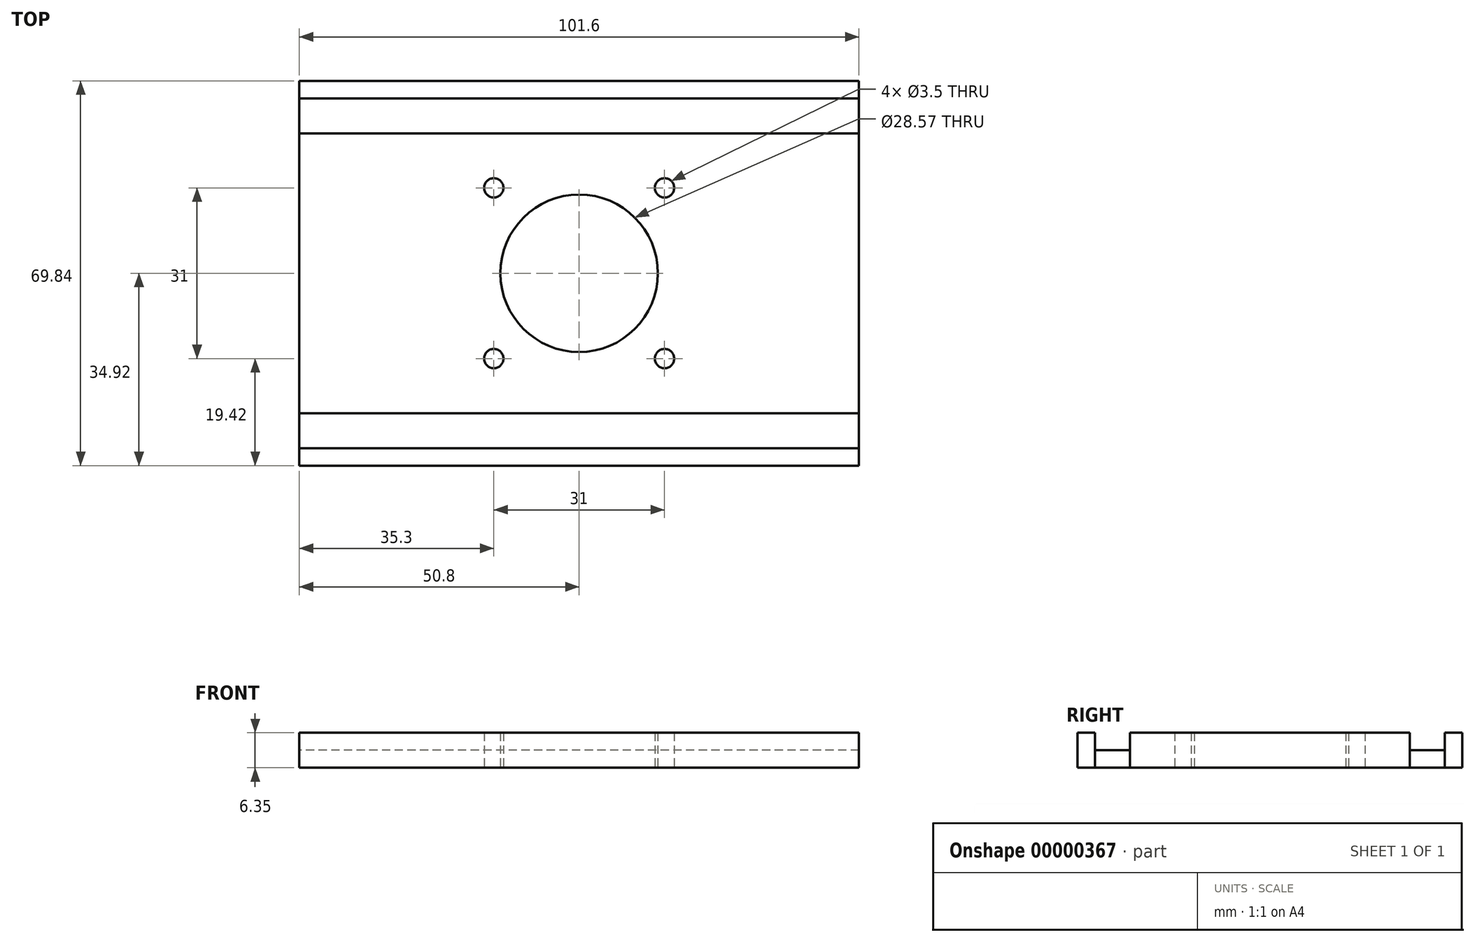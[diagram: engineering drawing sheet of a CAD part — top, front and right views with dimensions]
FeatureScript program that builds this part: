
annotation { "Feature Type Name" : "Feature", "Feature Type Description" : "" }
export const myFeature = defineFeature(function(context is Context, id is Id, definition is map)
    precondition{}
    {
        {
            var Q0;
            Q0=qCreatedBy(makeId("Top.planeOp"),FACE);
            var sketch = newSketch(context, id + "F0", { "sketchPlane" : qUnion([Q0])});
            skLineSegment(sketch, "E0.rect.bottom", {"start": v(50.8, -34.93) * mm, "end": v(-50.8, -34.93) * mm});
            skLineSegment(sketch, "E0.rect.top", {"start": v(50.8, 34.92) * mm, "end": v(-50.8, 34.93) * mm});
            skLineSegment(sketch, "E0.rect.left", {"start": v(50.8, -34.93) * mm, "end": v(50.8, 34.92) * mm});
            skLineSegment(sketch, "E0.rect.right", {"start": v(-50.8, -34.92) * mm, "end": v(-50.8, 34.92) * mm});
            skPoint(sketch, "E0.rect.middle", {"position": v(0, 0) * mm});
            skCircle(sketch, "E1", {"center": v(0, 0) * mm, "radius": 14.29 * mm});
            skLineSegment(sketch, "E2", {"start": v(-50.8, 31.75) * mm, "end": v(50.8, 31.75) * mm});
            skLineSegment(sketch, "E3", {"start": v(50.8, 31.75) * mm, "end": v(50.8, 25.4) * mm});
            skLineSegment(sketch, "E4", {"start": v(50.8, 25.4) * mm, "end": v(-50.8, 25.4) * mm});
            skLineSegment(sketch, "E5", {"start": v(-50.8, -25.4) * mm, "end": v(50.8, -25.4) * mm});
            skLineSegment(sketch, "E6", {"start": v(50.8, -25.4) * mm, "end": v(50.8, -31.75) * mm});
            skLineSegment(sketch, "E7", {"start": v(50.8, -31.75) * mm, "end": v(-50.8, -31.75) * mm});
            skLineSegment(sketch, "E8", {"start": v(0, 0) * mm, "end": v(0, 23.27) * mm, "construction": true});
            skLineSegment(sketch, "E9", {"start": v(0, 0) * mm, "end": v(-24.24, 0) * mm, "construction": true});
            skCircle(sketch, "E10", {"center": v(15.5, 15.5) * mm, "radius": 1.75 * mm});
            skCircle(sketch, "E11.0.MirrorC", {"center": v(-15.5, 15.5) * mm, "radius": 1.75 * mm});
            skCircle(sketch, "E12.0.MirrorC", {"center": v(15.5, -15.5) * mm, "radius": 1.75 * mm});
            skCircle(sketch, "E13.0.MirrorC", {"center": v(-15.5, -15.5) * mm, "radius": 1.75 * mm});
            skSolve(sketch);
        }
        {
            var Q0;
            {var subQ2=sQuery(id+"F0.wireOp",EDGE,"E0.rect.bottom");Q0=makeQuery(id+"F0.imprint","IMPRINT",FACE,{"disambiguationData":[TD([[makeQuery(id+"F0.imprint","IMPRINT",EDGE,{"derivedFrom":subQ2}),-1.0]])]});}
            var Q1;
            Q1=makeQuery(id+"F0.imprint","IMPRINT",FACE,{"disambiguationData":[TD([[makeQuery(id+"F0.imprint","IMPRINT",EDGE,{"derivedFrom":sQuery(id+"F0.wireOp",EDGE,"E1")}),-1.0]])]});
            var Q2;
            {var subQ2=sQuery(id+"F0.wireOp",EDGE,"E0.rect.top");Q2=makeQuery(id+"F0.imprint","IMPRINT",FACE,{"disambiguationData":[TD([[makeQuery(id+"F0.imprint","IMPRINT",EDGE,{"derivedFrom":subQ2}),1.0]])]});}
            extrude(context, id + "F1", {"entities" : qUnion([Q0, Q1, Q2]), "depth" : 6.35 * mm});
        }
        {
            var Q0;
            {var subQ1=sQuery(id+"F0.wireOp",EDGE,"E5");Q0=makeQuery(id+"F0.imprint","IMPRINT",FACE,{"disambiguationData":[TD([[makeQuery(id+"F0.imprint","IMPRINT",EDGE,{"derivedFrom":subQ1}),-1.0]])]});}
            var Q1;
            {var subQ1=sQuery(id+"F0.wireOp",EDGE,"E2");Q1=makeQuery(id+"F0.imprint","IMPRINT",FACE,{"disambiguationData":[TD([[makeQuery(id+"F0.imprint","IMPRINT",EDGE,{"derivedFrom":subQ1}),-1.0]])]});}
            extrude(context, id + "F2", {"entities" : qUnion([Q0, Q1]), "depth" : 3.17 * mm});
        }
    });
